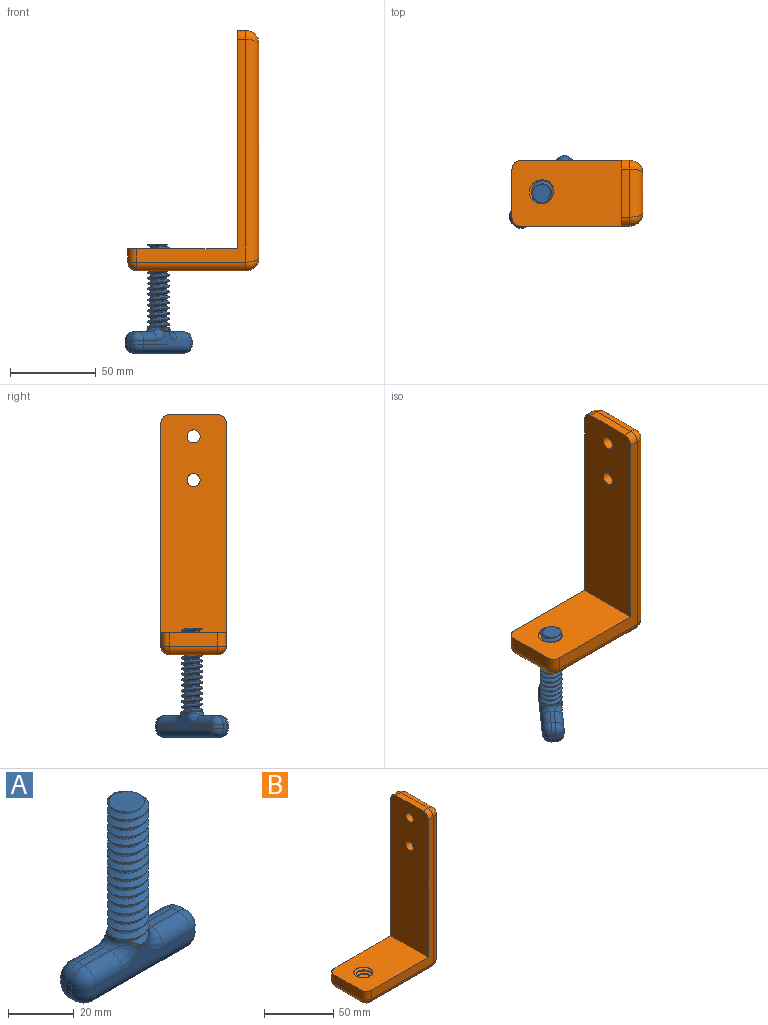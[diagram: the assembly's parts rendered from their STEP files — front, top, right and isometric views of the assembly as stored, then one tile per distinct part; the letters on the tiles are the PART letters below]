
ASSEMBLY  parts=2 mates=1
PART A: 62 faces, bbox 51.7x17.4x65.6 mm
  f0: cylinder r=6.35mm len=2.17mm, axis (0,0,-1), area 0.6mm2, adj f12,f13,f58,f60
  f1: cylinder r=6.35mm len=49.02mm, axis (0,0,-1), area 596.4mm2, adj f2,f10,f14,f15,f58,f60
  f2: plane 11.71x11.65mm, normal (0,0,1), area 91.5mm2, adj f1,f57,f58,f60
  f3: plane 11.52x2.54mm, normal (0,0,1), area 29.1mm2, adj f14,f20,f21,f22
  f4: plane 41.35x8.33mm, normal (0,1,0), area 136.5mm2, adj f16,f19,f20,f27,f30,f31,f38,f43
  f5: plane 2.54x2.54mm, normal (1,0,0), area 6.5mm2, adj f32,f39,f46,f49
  f6: plane 41.4x8.38mm, normal (0,-1,0), area 136.5mm2, adj f22,f23,f26,f33,f35,f37,f41,f49
  f7: plane 2.54x2.54mm, normal (-1,0,0), area 6.5mm2, adj f21,f40,f43,f52
  f8: plane 40.64x2.54mm, normal (0,0,-1), area 103.2mm2, adj f38,f39,f40,f41
  f9: plane 11.52x2.54mm, normal (0,0,1), area 29.1mm2, adj f11,f31,f32,f33
  f10: bspline ~6.41x2.66mm, area 3.5mm2, adj f1,f11,f27,f28,f55,f56
  f11: torus R=8.89mm, axis (0,0,-1), area 24.5mm2, adj f9,f10,f12,f30,f35,f56
  f12: bspline ~6.41x2.66mm, area 3.5mm2, adj f0,f11,f34,f37,f55,f56
  f13: bspline ~6.41x2.66mm, area 3.5mm2, adj f0,f14,f24,f26,f54,f59
  f14: torus R=8.89mm, axis (0,0,-1), area 24.5mm2, adj f1,f3,f13,f15,f19,f23,f59
  f15: bspline ~6.41x2.66mm, area 3.5mm2, adj f1,f14,f16,f18,f59
  f16: bspline ~2.83x1.76mm, area 1.2mm2, adj f4,f15,f17
  f17: bspline ~1.67x1.42mm, area 0.4mm2, adj f16,f18,f19
  f18: bspline ~1.92x1.35mm, area 0.7mm2, adj f15,f17,f19
  f19: bspline ~9.39x6.92mm, area 40.7mm2, adj f4,f14,f17,f18,f20
  f20: cylinder r=5.08mm len=11.52mm, axis (1,0,0), area 91.9mm2, adj f3,f4,f19,f42
  f21: cylinder r=5.08mm len=5.08mm, axis (0,1,0), area 20.3mm2, adj f3,f7,f42,f51
  f22: cylinder r=5.08mm len=11.52mm, axis (-1,0,0), area 91.9mm2, adj f3,f6,f23,f51
  f23: bspline ~9.39x6.92mm, area 40.8mm2, adj f6,f14,f22,f24,f25
  f24: bspline ~1.92x1.35mm, area 0.7mm2, adj f13,f23,f25
  f25: bspline ~1.67x1.42mm, area 0.4mm2, adj f23,f24,f26
  f26: bspline ~2.83x1.76mm, area 1.2mm2, adj f6,f13,f25
  f27: bspline ~2.82x1.75mm, area 1.2mm2, adj f4,f10,f29
  f28: bspline ~1.93x1.35mm, area 0.7mm2, adj f10,f29,f30
  f29: bspline ~1.66x1.41mm, area 0.4mm2, adj f27,f28,f30
  f30: bspline ~9.39x6.92mm, area 40.7mm2, adj f4,f11,f28,f29,f31
  f31: cylinder r=5.08mm len=11.52mm, axis (1,0,0), area 91.9mm2, adj f4,f9,f30,f45
  f32: cylinder r=5.08mm len=5.08mm, axis (0,-1,0), area 20.3mm2, adj f5,f9,f45,f48
  f33: cylinder r=5.08mm len=11.52mm, axis (-1,0,0), area 91.9mm2, adj f6,f9,f35,f48
  f34: bspline ~1.93x1.35mm, area 0.7mm2, adj f12,f35,f36
  f35: bspline ~9.39x6.92mm, area 40.8mm2, adj f6,f11,f33,f34,f36
  f36: bspline ~1.66x1.41mm, area 0.4mm2, adj f34,f35,f37
  f37: bspline ~2.82x1.75mm, area 1.2mm2, adj f6,f12,f36
  f38: cylinder r=5.08mm len=40.64mm, axis (-1,0,0), area 324.3mm2, adj f4,f8,f44,f47
  f39: cylinder r=5.08mm len=5.08mm, axis (0,1,0), area 20.3mm2, adj f5,f8,f47,f50
  f40: cylinder r=5.08mm len=5.08mm, axis (0,-1,0), area 20.3mm2, adj f7,f8,f44,f53
  f41: cylinder r=5.08mm len=40.64mm, axis (1,0,0), area 324.3mm2, adj f6,f8,f50,f53
  f42: sphere r=5.08mm, area 40.5mm2, adj f20,f21,f43
  f43: cylinder r=5.08mm len=5.08mm, axis (0,0,1), area 20.3mm2, adj f4,f7,f42,f44
  f44: sphere r=5.08mm, area 40.5mm2, adj f38,f40,f43
  f45: sphere r=5.08mm, area 40.5mm2, adj f31,f32,f46
  f46: cylinder r=5.08mm len=5.08mm, axis (0,0,-1), area 20.3mm2, adj f4,f5,f45,f47
  f47: sphere r=5.08mm, area 40.5mm2, adj f38,f39,f46
  f48: sphere r=5.08mm, area 40.5mm2, adj f32,f33,f49
  f49: cylinder r=5.08mm len=5.08mm, axis (0,0,1), area 20.3mm2, adj f5,f6,f48,f50
  f50: sphere r=5.08mm, area 40.5mm2, adj f39,f41,f49
  f51: sphere r=5.08mm, area 40.5mm2, adj f21,f22,f52
  f52: cylinder r=5.08mm len=5.08mm, axis (0,0,-1), area 20.3mm2, adj f6,f7,f51,f53
  f53: sphere r=5.08mm, area 40.5mm2, adj f40,f41,f52
  f54: cylinder r=6.35mm len=4.53mm, axis (0,0,1), area 0.9mm2, adj f13,f58,f61
  f55: cylinder r=6.35mm len=12.7mm, axis (0,0,1), area 21.1mm2, adj f10,f12,f58,f61
  f56: cylinder r=6.35mm len=11.77mm, axis (0,0,1), area 12.6mm2, adj f10,f11,f12,f60
  f57: bspline ~53.18x10.7mm, area 403.5mm2, adj f2,f58,f60,f61
  f58: bspline ~53.38x14.66mm, area 1096.5mm2, adj f0,f1,f2,f54,f55,f57,f59,f61
  f59: cylinder r=6.35mm len=12.63mm, axis (0,0,1), area 35.9mm2, adj f13,f14,f15,f58,f60,f61
  f60: bspline ~52.85x14.66mm, area 1101.5mm2, adj f0,f1,f2,f56,f57,f59,f61
  f61: plane 13.55x13.55mm, normal (0,0,1), area 35.2mm2, adj f54,f55,f57,f58,f59,f60
PART B: 31 faces, bbox 77.1x39x142.1 mm
  f0: plane 64.39x38.99mm, normal (0,0,1), area 2261.9mm2, adj f2,f4,f5,f6,f10,f11,f12,f13
  f1: plane 64.39x28.83mm, normal (0,0,-1), area 1627.9mm2, adj f10,f11,f12,f13,f14,f23,f25,f28
  f2: plane 129.54x63.5mm, normal (0,-1,0), area 1103.2mm2, adj f0,f6,f15,f21,f23,f30
  f3: plane 124.46x22.86mm, normal (1,0,0), area 2753.9mm2, adj f8,f9,f14,f15,f16,f17
  f4: plane 129.54x63.5mm, normal (0,1,0), area 1103.2mm2, adj f0,f6,f16,f19,f25,f26
  f5: plane 27.94x7.62mm, normal (-1,0,0), area 212.9mm2, adj f0,f26,f28,f30
  f6: plane 127x38.1mm, normal (-1,0,0), area 4736.4mm2, adj f0,f2,f4,f7,f8,f9,f19,f21
  f7: plane 27.94x5.08mm, normal (0,0,1), area 141.9mm2, adj f6,f17,f19,f21
  f8: cylinder r=3.81mm len=12.7mm, axis (1,0,0), area 304mm2, adj f3,f6
  f9: cylinder r=3.81mm len=12.7mm, axis (1,0,0), area 304mm2, adj f3,f6
  f10: bspline ~17.9x15.5mm, area 344.7mm2, adj f0,f1,f12,f13
  f11: bspline ~17.9x15.5mm, area 344.3mm2, adj f0,f1,f12,f13
  f12: bspline ~18.23x15.79mm, area 90.4mm2, adj f0,f1,f10,f11
  f13: cylinder r=6.03mm len=12.7mm, axis (0,0,-1), area 121.4mm2, adj f0,f1,f10,f11
  f14: cylinder r=7.62mm len=27.94mm, axis (0,1,0), area 304mm2, adj f1,f3,f22,f24
  f15: cylinder r=7.62mm len=129.54mm, axis (0,0,1), area 1520.1mm2, adj f2,f3,f20,f22
  f16: cylinder r=7.62mm len=129.54mm, axis (0,0,-1), area 1520.1mm2, adj f3,f4,f18,f24
  f17: cylinder r=7.62mm len=27.94mm, axis (0,-1,0), area 304mm2, adj f3,f7,f18,f20
  f18: bspline ~8.04x7.62mm, area 62.9mm2, adj f16,f17,f19
  f19: cylinder r=5.08mm len=5.08mm, axis (1,0,0), area 40.5mm2, adj f4,f6,f7,f18
  f20: bspline ~9.26x7.62mm, area 62.9mm2, adj f15,f17,f21
  f21: cylinder r=5.08mm len=5.08mm, axis (-1,0,0), area 40.5mm2, adj f2,f6,f7,f20
  f22: bspline ~9.26x7.62mm, area 62.9mm2, adj f14,f15,f23
  f23: cylinder r=5.08mm len=63.5mm, axis (1,0,0), area 506.7mm2, adj f1,f2,f22,f29
  f24: bspline ~9.26x7.62mm, area 62.9mm2, adj f14,f16,f25
  f25: cylinder r=5.08mm len=63.5mm, axis (-1,0,0), area 506.7mm2, adj f1,f4,f24,f27
  f26: cylinder r=5.08mm len=7.62mm, axis (0,0,1), area 60.8mm2, adj f0,f4,f5,f27
  f27: sphere r=5.08mm, area 40.5mm2, adj f25,f26,f28
  f28: cylinder r=5.08mm len=27.94mm, axis (0,-1,0), area 223mm2, adj f1,f5,f27,f29
  f29: sphere r=5.08mm, area 40.5mm2, adj f23,f28,f30
  f30: cylinder r=5.08mm len=7.62mm, axis (0,0,-1), area 60.8mm2, adj f0,f2,f5,f29
PLACE A rot(axis=(0,0,1),48.4deg) t=(-39.91,19.66,-34.14)mm
PLACE B t=(-19.62,18.75,1.21)mm fixed
MATE cylindrical A.f2 <-> B.f13  axis (0,0,1) through (-40.23,18.75,16.66)mm
